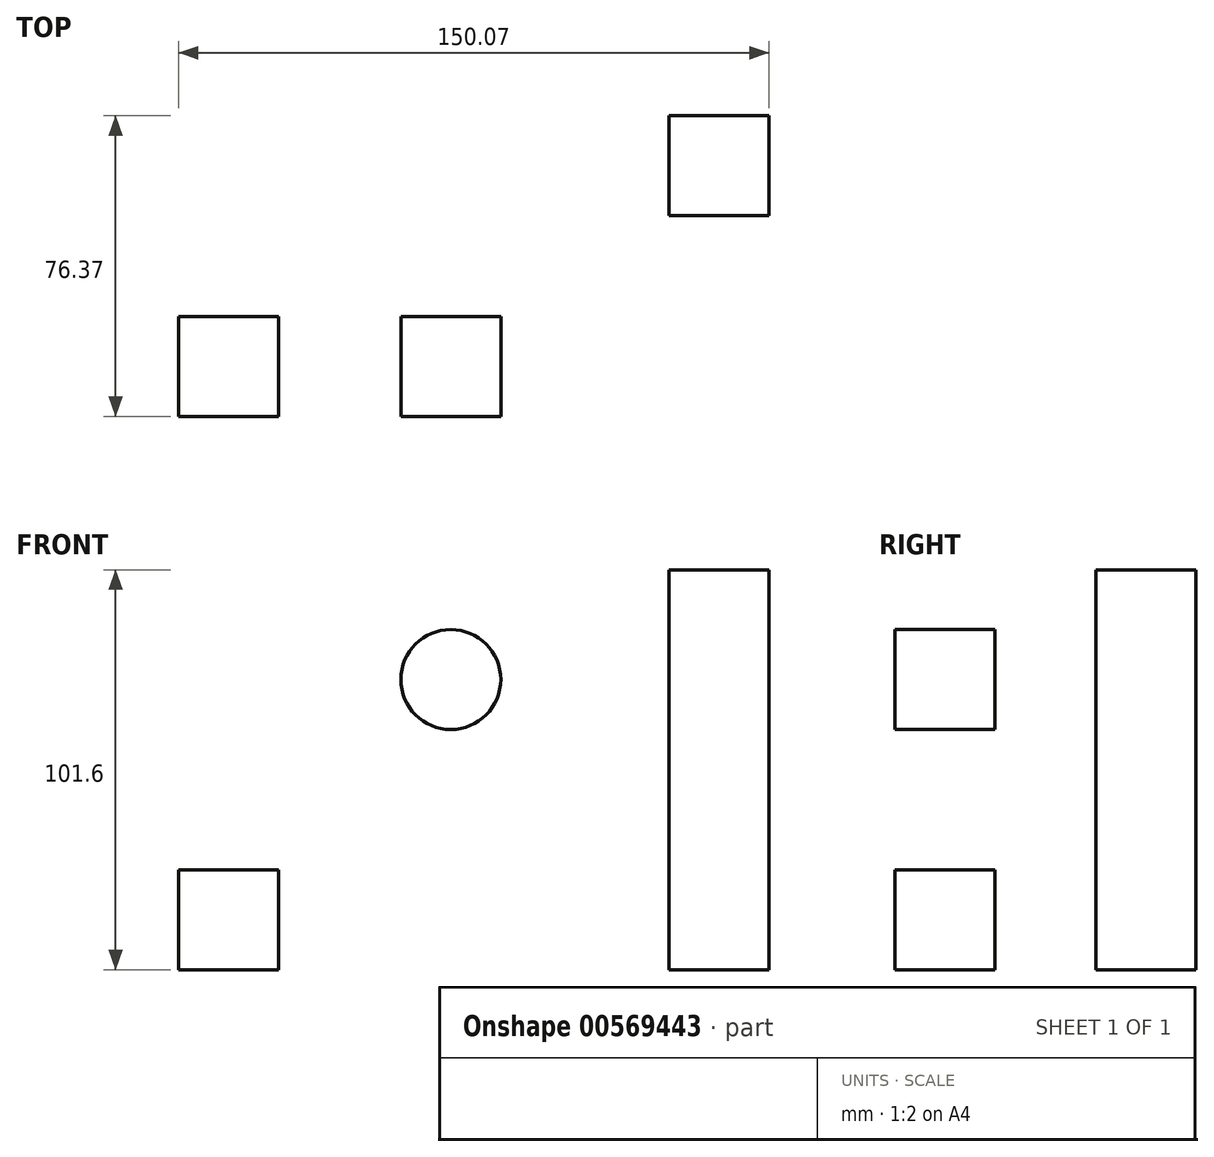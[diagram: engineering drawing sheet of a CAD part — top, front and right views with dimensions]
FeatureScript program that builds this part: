
annotation { "Feature Type Name" : "Feature", "Feature Type Description" : "" }
export const myFeature = defineFeature(function(context is Context, id is Id, definition is map)
    precondition{}
    {
        {
            var Q0;
            Q0=qCreatedBy(makeId("Front.planeOp"),FACE);
            var sketch = newSketch(context, id + "F0", { "sketchPlane" : qUnion([Q0])});
            skLineSegment(sketch, "E0.bottom", {"start": v(-52.23, 25.4) * mm, "end": v(-26.83, 25.4) * mm});
            skLineSegment(sketch, "E0.top", {"start": v(-52.23, 0) * mm, "end": v(-26.83, 0) * mm});
            skLineSegment(sketch, "E0.left", {"start": v(-52.23, 25.4) * mm, "end": v(-52.23, 0) * mm});
            skLineSegment(sketch, "E0.right", {"start": v(-26.83, 25.4) * mm, "end": v(-26.83, 0) * mm});
            skSolve(sketch);
        }
        {
            var Q0;
            Q0=makeQuery(id+"F0.imprint","IMPRINT",FACE,{"disambiguationData":[TD([[makeQuery(id+"F0.imprint","IMPRINT",EDGE,{"derivedFrom":sQuery(id+"F0.wireOp",EDGE,"E0.bottom")}),-1.0]])]});
            extrude(context, id + "F1", {"entities" : qUnion([Q0]), "depth" : 25.4 * mm, "offsetDistance" : 25.4 * mm});
        }
        {
            var Q0;
            Q0=qCreatedBy(makeId("Top.planeOp"),FACE);
            var sketch = newSketch(context, id + "F2", { "sketchPlane" : qUnion([Q0])});
            skLineSegment(sketch, "E1.bottom", {"start": v(72.44, 50.97) * mm, "end": v(97.84, 50.97) * mm});
            skLineSegment(sketch, "E1.top", {"start": v(72.44, 25.57) * mm, "end": v(97.84, 25.57) * mm});
            skLineSegment(sketch, "E1.left", {"start": v(72.44, 50.97) * mm, "end": v(72.44, 25.57) * mm});
            skLineSegment(sketch, "E1.right", {"start": v(97.84, 50.97) * mm, "end": v(97.84, 25.57) * mm});
            skSolve(sketch);
        }
        {
            var Q0;
            Q0=makeQuery(id+"F2.imprint","IMPRINT",FACE,{"disambiguationData":[TD([[makeQuery(id+"F2.imprint","IMPRINT",EDGE,{"derivedFrom":sQuery(id+"F2.wireOp",EDGE,"E1.bottom")}),-1.0]])]});
            extrude(context, id + "F3", {"entities" : qUnion([Q0]), "depth" : 101.6 * mm, "offsetDistance" : 25.4 * mm});
        }
        {
            var Q0;
            Q0=qCreatedBy(makeId("Front.planeOp"),FACE);
            var sketch = newSketch(context, id + "F4", { "sketchPlane" : qUnion([Q0])});
            skCircle(sketch, "E2", {"center": v(16.96, 73.74) * mm, "radius": 12.7 * mm});
            skSolve(sketch);
        }
        {
            var Q0;
            Q0=makeQuery(id+"F4.imprint","IMPRINT",FACE,{"disambiguationData":[TD([[makeQuery(id+"F4.imprint","IMPRINT",EDGE,{"derivedFrom":sQuery(id+"F4.wireOp",EDGE,"E2")}),1.0]])]});
            extrude(context, id + "F5", {"entities" : qUnion([Q0]), "depth" : 25.4 * mm, "offsetDistance" : 25.4 * mm});
        }
    });
